# Revit family: Seating-LAMMHULTS-CAROUSEL-Swivel_Base-4_Feet
name_source: partatom
category: Furniture
revit_build: Autodesk Revit 2017 (Build: 20170816_0615(x64)
units: mm (PartAtom-declared; Revit-internal decimal feet)

## family parameters
Always vertical = Yes
Cut with Voids When Loaded = No
OmniClass Number = 23.40.20.00
OmniClass Title = General Furniture and Specialties
Room Calculation Point = No
Shared = No
Work Plane-Based = No

## types (5) — shared parameters
Assembly Code = E2020
Description = *Please enter mtrl description here for use in mto*
Height = 810 mm
Keynote = 46.B
Manufacturer = LAMMHULTS
Model = CAROUSEL
URL = www.lammhults.se
Width = 620 mm  [stored 2.03412 ft]

## per-type parameters (varying)
| type | Back Inside Primary Material | Back Inside Secondary Material | Back Outside Material | Feet Material | Frame Material | Legs Material | Seat Material | Two Colored Back |
| 2 Colour Lether White Fabric Purple | Leather - White | Fabric - Dark Purple Woven | Leather - White | Metal - Black - Matte | Metal - Chrome - Polished | Metal - Black - Matte | Fabric - Dark Purple Woven | Yes |
| 2 Colour Lether Black Fabric Grey | Leather - Black | Leather - Black | Fabric - Grey Woven | Metal - Chrome - Polished | Metal - Black - Matte | Metal - Black - Matte | Fabric - Grey Woven | Yes |
| 1 Colour  Fabric Grey | Fabric - Grey Woven | Fabric - Grey Woven | Fabric - Grey Woven | Metal - Chrome - Polished | Metal - Chrome - Polished | Metal - Black - Matte | Fabric - Grey Woven | No |
| 1 Colour  Fabric Blue | Fabric - Dark Blue Woven | Fabric - Dark Blue Woven | Fabric - Dark Blue Woven | Metal - Black - Matte | Metal - Black - Matte | Metal - Black - Matte | Fabric - Dark Blue Woven | No |
| 1 Colour  Fabric Orange | Fabric - Orange | Fabric - Orange | Fabric - Orange | Metal - Chrome - Polished | Metal - Chrome - Polished | Colour - Orange | Fabric - Orange | No |

note: [stored X ft] marks values corroborated as IEEE doubles in the binary element streams (Revit-internal decimal feet)

## geometry (parser evidence)
native form markers: Blend x14, Sweep x2
no freeform markers — native parametric forms only
